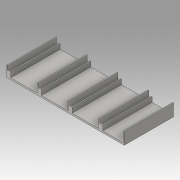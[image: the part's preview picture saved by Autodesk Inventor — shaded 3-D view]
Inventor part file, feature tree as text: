
AUTODESK INVENTOR PART (.ipt)
format: ipt  version: 2016 (Build 200138000, 138)  size: 215,040 bytes
history: native  units: in
note: dims shown in document units (in); Inventor stores cm internally (conversion verified against a paired STEP export)
features: sketch x15, extrude x14
ambient origin geometry x8: Origin, YZ Plane, XZ Plane, XY Plane, X Axis, Y Axis, Z Axis, Center Point
bodies: Solid1 (feature_tree)
feature tree (29):
  extrude  "Extrusion1"  Depth=3.4in TaperAngle=0.0deg
  extrude  "Extrusion2"  Depth=0.6in TaperAngle=0.0deg
  extrude  "Extrusion3"  Depth=0.34in TaperAngle=0.0deg
  extrude  "Extrusion4"  Depth=0.6in TaperAngle=0.0deg
  extrude  "Extrusion5"  Depth=0.34in TaperAngle=0.0deg
  extrude  "Extrusion6"  Depth=0.6in TaperAngle=0.0deg
  extrude  "Extrusion7"  Depth=0.34in TaperAngle=0.0deg
  extrude  "Extrusion8"  Depth=0.6in TaperAngle=0.0deg
  extrude  "Extrusion9"  Depth=0.34in TaperAngle=0.0deg
  extrude  "Extrusion10"  Depth=0.34in TaperAngle=0.0deg
  extrude  "Extrusion11"  Depth=0.34in TaperAngle=0.0deg
  extrude  "Extrusion12"  Depth=0.063in
  extrude  "Extrusion13"  [1 undecoded]
  sketch  "Sketch14"
  extrude  "Extrusion14"  [1 undecoded]
  sketch  "Sketch1"  dims[d0=8.126in d1=3.4in d2=0.0in]
  sketch  "Sketch2"  dims[d3=0.063in d4=0.6in d5=0.0in]
  sketch  "Sketch3"  dims[d6=0.063in d7=0.34in d8=0.0in]
  sketch  "Sketch4"  dims[d9=0.063in d10=0.6in d11=0.0in]
  sketch  "Sketch5"  dims[d12=0.063in d13=0.34in d14=0.0in]
  sketch  "Sketch6"  dims[d15=0.063in d16=0.6in d17=0.0in]
  sketch  "Sketch7"  dims[d18=0.063in d19=0.34in d20=0.0in]
  sketch  "Sketch8"  dims[d21=0.063in d22=0.6in d23=0.0in]
  sketch  "Sketch9"  dims[d24=0.063in d25=0.34in d26=0.0in]
  sketch  "Sketch10"  dims[d27=0.063in d28=0.34in d29=0.0in]
  sketch  "Sketch11"  dims[d30=0.34in d31=0.0in d32=0.34in d33=0.0in]
  sketch  "Sketch12"  dims[d34=0.34in d35=0.0in d36=0.063in]
  sketch  "Sketch13"  dims[d37=0.718in d38=0.0in]
  sketch  "Sketch15"
note: 2 required parameter values undecoded (feature->parameter linkage not recoverable at this tier; creation-order binding heuristic only, values carry confidence <= 0.55)
